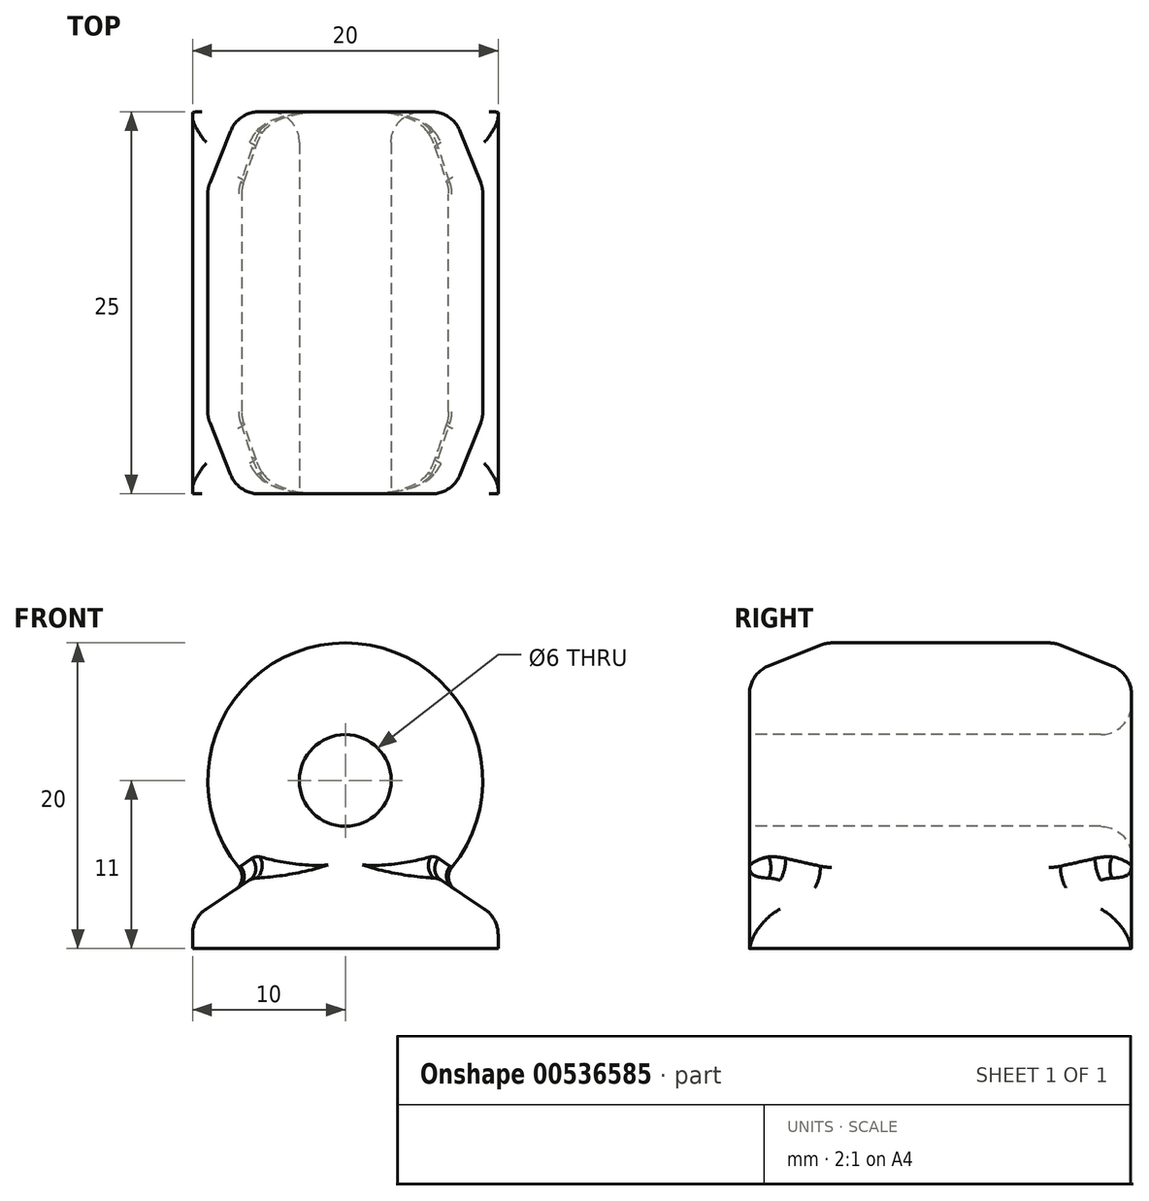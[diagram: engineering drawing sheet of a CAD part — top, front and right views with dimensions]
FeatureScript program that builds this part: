
annotation { "Feature Type Name" : "Feature", "Feature Type Description" : "" }
export const myFeature = defineFeature(function(context is Context, id is Id, definition is map)
    precondition{}
    {
        {
            var Q0;
            Q0=qCreatedBy(makeId("Front.planeOp"),FACE);
            var sketch = newSketch(context, id + "F0", { "sketchPlane" : qUnion([Q0])});
            skLineSegment(sketch, "E0.bottom", {"start": v(10, -1) * mm, "end": v(-10, -1) * mm});
            skLineSegment(sketch, "E0.left", {"start": v(10, -1) * mm, "end": v(10, 1) * mm});
            skLineSegment(sketch, "E0.right", {"start": v(-10, -1) * mm, "end": v(-10, 1) * mm});
            skPoint(sketch, "E0.middle", {"position": v(0, 0) * mm});
            skLineSegment(sketch, "E1", {"start": v(0, 0) * mm, "end": v(0, 10) * mm, "construction": true});
            skPoint(sketch, "E1.endSnap0", {"position": v(0, 1) * mm});
            skArc(sketch, "E2", {"start": v(6.22, 3.5) * mm, "mid": v(0, 19) * mm, "end": v(-6.22, 3.5) * mm});
            skPoint(sketch, "E3", {"position": v(0, 3.5) * mm});
            skLineSegment(sketch, "E4", {"start": v(-8.61, 3.5) * mm, "end": v(8.15, 3.5) * mm, "construction": true});
            skLineSegment(sketch, "E5", {"start": v(-10, 1) * mm, "end": v(-6.22, 3.5) * mm});
            skLineSegment(sketch, "E6", {"start": v(10, 1) * mm, "end": v(6.22, 3.5) * mm});
            skSolve(sketch);
        }
        {
            var Q0;
            Q0=makeQuery(id+"F0.imprint","IMPRINT",FACE,{"disambiguationData":[TD([[makeQuery(id+"F0.imprint","IMPRINT",EDGE,{"derivedFrom":sQuery(id+"F0.wireOp",EDGE,"E0.bottom")}),-1.0]])]});
            extrude(context, id + "F1", {"entities" : qUnion([Q0]), "endBound" : BoundingType.SYMMETRIC, "depth" : 25 * mm, "offsetDistance" : 25 * mm});
        }
        {
            var Q0;
            Q0=makeQuery(id+"F1.opExtrude","CAP_FACE",FACE,{"disambiguationData":[OSD([sQuery(id+"F0.wireOp",EDGE,"E0.bottom"),sQuery(id+"F0.wireOp",EDGE,"E0.left"),sQuery(id+"F0.wireOp",EDGE,"E0.right"),sQuery(id+"F0.wireOp",EDGE,"E2"),sQuery(id+"F0.wireOp",EDGE,"E5"),sQuery(id+"F0.wireOp",EDGE,"E6")])],"isStart":false});
            var sketch = newSketch(context, id + "F2", { "sketchPlane" : qUnion([Q0])});
            skCircle(sketch, "E7", {"center": v(0, 10) * mm, "radius": 3 * mm});
            skSolve(sketch);
        }
        {
            var Q0;
            Q0=makeQuery(id+"F2.imprint","IMPRINT",FACE,{"disambiguationData":[TD([[makeQuery(id+"F2.imprint","IMPRINT",EDGE,{"derivedFrom":sQuery(id+"F2.wireOp",EDGE,"E7")}),1.0]])]});
            extrude(context, id + "F3", {"entities" : qUnion([Q0]), "operationType" : NewBodyOperationType.REMOVE, "oppositeDirection" : true, "depth" : 30 * mm, "offsetDistance" : 25 * mm});
        }
        {
            var Q0;
            Q0=makeQuery(id+"F1.opExtrude","CAP_EDGE",EDGE,{"disambiguationData":[OSD([sQuery(id+"F0.wireOp",EDGE,"E2")])],"isStart":true});
            var Q1;
            Q1=makeQuery(id+"F1.opExtrude","CAP_EDGE",EDGE,{"disambiguationData":[OSD([sQuery(id+"F0.wireOp",EDGE,"E2")])],"isStart":false});
            chamfer(context, id + "F4", {"entities" : qUnion([Q0, Q1]), "chamferType" : ChamferType.TWO_OFFSETS, "width1" : 5 * mm, "oppositeDirection" : false, "width2" : 2 * mm, "tangentPropagation" : true});
        }
        {
            var Q0;
            Q0=makeQuery(id+"F3.boolean.opBoolean","COPY",EDGE,{"derivedFrom":makeQuery(id+"F3.opExtrude","CAP_EDGE",EDGE,{"disambiguationData":[OSD([sQuery(id+"F2.wireOp",EDGE,"E7")])],"isStart":true})});
            var Q1;
            Q1=makeQuery(id+"F3.boolean.opBoolean","INTERSECT",EDGE,{"derivedFrom":[makeQuery(id+"F1.opExtrude","CAP_FACE",FACE,{"disambiguationData":[OSD([sQuery(id+"F0.wireOp",EDGE,"E0.bottom"),sQuery(id+"F0.wireOp",EDGE,"E0.left"),sQuery(id+"F0.wireOp",EDGE,"E0.right"),sQuery(id+"F0.wireOp",EDGE,"E2"),sQuery(id+"F0.wireOp",EDGE,"E5"),sQuery(id+"F0.wireOp",EDGE,"E6")])],"isStart":true}),makeQuery(id+"F3.opExtrude","SWEPT_FACE",FACE,{"disambiguationData":[OSD([sQuery(id+"F2.wireOp",EDGE,"E7")])]})]});
            var Q2;
            {var subQ0=sQuery(id+"F0.wireOp",EDGE,"E2");Q2=makeQuery(id+"F4.opChamfer","BLEND_EDGE",EDGE,{"blendedFrom":[makeQuery(id+"F1.opExtrude","CAP_EDGE",EDGE,{"disambiguationData":[OSD([subQ0])],"isStart":true}),makeQuery(id+"F1.opExtrude","CAP_FACE",FACE,{"disambiguationData":[OSD([sQuery(id+"F0.wireOp",EDGE,"E0.bottom"),sQuery(id+"F0.wireOp",EDGE,"E0.left"),sQuery(id+"F0.wireOp",EDGE,"E0.right"),subQ0,sQuery(id+"F0.wireOp",EDGE,"E5"),sQuery(id+"F0.wireOp",EDGE,"E6")])],"isStart":true})],"blendedInto":[makeQuery(id+"F1.opExtrude","CAP_FACE",FACE,{"disambiguationData":[OSD([sQuery(id+"F0.wireOp",EDGE,"E0.bottom"),sQuery(id+"F0.wireOp",EDGE,"E0.left"),sQuery(id+"F0.wireOp",EDGE,"E0.right"),subQ0,sQuery(id+"F0.wireOp",EDGE,"E5"),sQuery(id+"F0.wireOp",EDGE,"E6")])],"isStart":true})]});}
            var Q3;
            {var subQ0=sQuery(id+"F0.wireOp",EDGE,"E2");Q3=makeQuery(id+"F4.opChamfer","BLEND_EDGE",EDGE,{"blendedFrom":[makeQuery(id+"F1.opExtrude","CAP_EDGE",EDGE,{"disambiguationData":[OSD([subQ0])],"isStart":false}),makeQuery(id+"F1.opExtrude","CAP_FACE",FACE,{"disambiguationData":[OSD([sQuery(id+"F0.wireOp",EDGE,"E0.bottom"),sQuery(id+"F0.wireOp",EDGE,"E0.left"),sQuery(id+"F0.wireOp",EDGE,"E0.right"),subQ0,sQuery(id+"F0.wireOp",EDGE,"E5"),sQuery(id+"F0.wireOp",EDGE,"E6")])],"isStart":false})],"blendedInto":[makeQuery(id+"F1.opExtrude","CAP_FACE",FACE,{"disambiguationData":[OSD([sQuery(id+"F0.wireOp",EDGE,"E0.bottom"),sQuery(id+"F0.wireOp",EDGE,"E0.left"),sQuery(id+"F0.wireOp",EDGE,"E0.right"),subQ0,sQuery(id+"F0.wireOp",EDGE,"E5"),sQuery(id+"F0.wireOp",EDGE,"E6")])],"isStart":false})]});}
            var Q4;
            {var subQ0=sQuery(id+"F0.wireOp",EDGE,"E2");Q4=makeQuery(id+"F4.opChamfer","BLEND_EDGE",EDGE,{"blendedFrom":[makeQuery(id+"F1.opExtrude","CAP_EDGE",EDGE,{"disambiguationData":[OSD([subQ0])],"isStart":false}),makeQuery(id+"F1.opExtrude","SWEPT_FACE",FACE,{"disambiguationData":[OSD([subQ0])]})],"blendedInto":[makeQuery(id+"F1.opExtrude","SWEPT_FACE",FACE,{"disambiguationData":[OSD([subQ0])]})]});}
            var Q5;
            {var subQ0=sQuery(id+"F0.wireOp",EDGE,"E2");Q5=makeQuery(id+"F4.opChamfer","BLEND_EDGE",EDGE,{"blendedFrom":[makeQuery(id+"F1.opExtrude","CAP_EDGE",EDGE,{"disambiguationData":[OSD([subQ0])],"isStart":true}),makeQuery(id+"F1.opExtrude","SWEPT_FACE",FACE,{"disambiguationData":[OSD([subQ0])]})],"blendedInto":[makeQuery(id+"F1.opExtrude","SWEPT_FACE",FACE,{"disambiguationData":[OSD([subQ0])]})]});}
            fillet(context, id + "F5", {"entities" : qUnion([Q0, Q1, Q2, Q3, Q4, Q5]), "radius" : 2 * mm, "tangentPropagation" : true, "allowEdgeOverflow" : false});
        }
        {
            var Q0;
            Q0=makeQuery(id+"F1.opExtrude","CAP_EDGE",EDGE,{"disambiguationData":[OSD([sQuery(id+"F0.wireOp",EDGE,"E6")])],"isStart":true});
            var Q1;
            Q1=makeQuery(id+"F1.opExtrude","SWEPT_EDGE",EDGE,{"disambiguationData":[OSD([sQuery(id+"F0.wireOp",EDGE,"E0.left"),sQuery(id+"F0.wireOp",EDGE,"E6")])]});
            var Q2;
            Q2=makeQuery(id+"F1.opExtrude","CAP_EDGE",EDGE,{"disambiguationData":[OSD([sQuery(id+"F0.wireOp",EDGE,"E6")])],"isStart":false});
            var Q3;
            Q3=makeQuery(id+"F1.opExtrude","CAP_EDGE",EDGE,{"disambiguationData":[OSD([sQuery(id+"F0.wireOp",EDGE,"E5")])],"isStart":false});
            var Q4;
            Q4=makeQuery(id+"F1.opExtrude","SWEPT_EDGE",EDGE,{"disambiguationData":[OSD([sQuery(id+"F0.wireOp",EDGE,"E0.right"),sQuery(id+"F0.wireOp",EDGE,"E5")])]});
            var Q5;
            Q5=makeQuery(id+"F1.opExtrude","CAP_EDGE",EDGE,{"disambiguationData":[OSD([sQuery(id+"F0.wireOp",EDGE,"E5")])],"isStart":true});
            fillet(context, id + "F6", {"entities" : qUnion([Q0, Q1, Q2, Q3, Q4, Q5]), "radius" : 2 * mm, "tangentPropagation" : true, "allowEdgeOverflow" : false});
        }
        {
            var Q0;
            Q0=makeQuery(id+"F4.opChamfer","BLEND_EDGE",EDGE,{"blendedFrom":[makeQuery(id+"F1.opExtrude","CAP_EDGE",EDGE,{"disambiguationData":[OSD([sQuery(id+"F0.wireOp",EDGE,"E2")])],"isStart":false}),makeQuery(id+"F1.opExtrude","SWEPT_FACE",FACE,{"disambiguationData":[OSD([sQuery(id+"F0.wireOp",EDGE,"E6")])]})],"blendedInto":[makeQuery(id+"F1.opExtrude","SWEPT_FACE",FACE,{"disambiguationData":[OSD([sQuery(id+"F0.wireOp",EDGE,"E6")])]})]});
            var Q1;
            Q1=makeQuery(id+"F1.opExtrude","SWEPT_EDGE",EDGE,{"disambiguationData":[OSD([sQuery(id+"F0.wireOp",EDGE,"E2"),sQuery(id+"F0.wireOp",EDGE,"E5")])]});
            fillet(context, id + "F7", {"entities" : qUnion([Q0, Q1]), "radius" : 1 * mm, "tangentPropagation" : true, "allowEdgeOverflow" : false});
        }
    });
